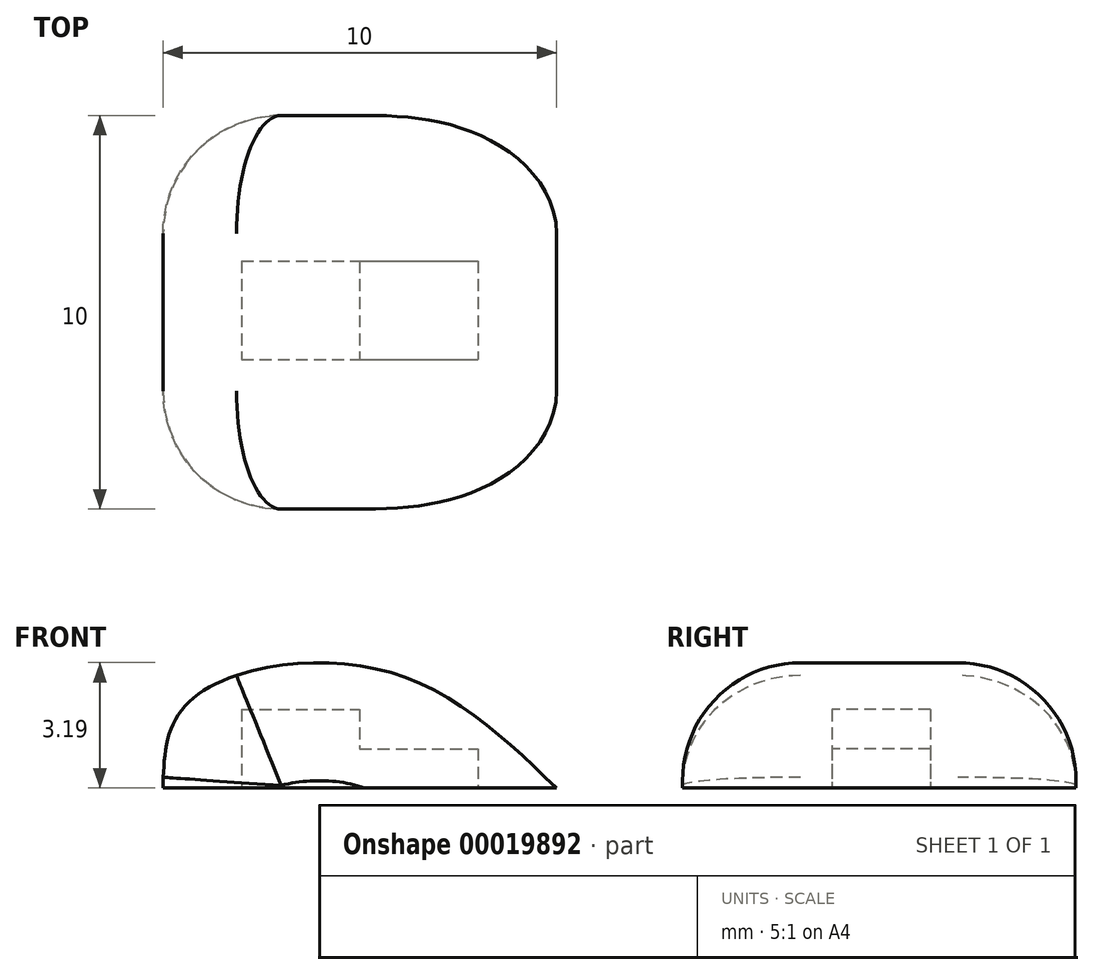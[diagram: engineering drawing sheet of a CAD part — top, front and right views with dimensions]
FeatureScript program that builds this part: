
annotation { "Feature Type Name" : "Feature", "Feature Type Description" : "" }
export const myFeature = defineFeature(function(context is Context, id is Id, definition is map)
    precondition{}
    {
        {
            var Q0;
            Q0=qCreatedBy(makeId("Front.planeOp"),FACE);
            var sketch = newSketch(context, id + "F0", { "sketchPlane" : qUnion([Q0])});
            skLineSegment(sketch, "E0", {"start": v(-11.41, -9.36) * mm, "end": v(-1.41, -9.36) * mm});
            skFitSpline(sketch, "E1", {"points": [v(-11.41, -9.36) * mm, v(-10.74, -7.16) * mm, v(-5.93, -6.34) * mm, v(-1.41, -9.36) * mm], "startDerivative": vector(0.3, 9.7) * mm, "endDerivative": vector(10.47, -10.1) * mm});
            skSolve(sketch);
        }
        {
            var Q0;
            Q0=makeQuery(id+"F0.imprint","IMPRINT",FACE,{"disambiguationData":[TD([[makeQuery(id+"F0.imprint","IMPRINT",EDGE,{"derivedFrom":sQuery(id+"F0.wireOp",EDGE,"E0")}),1.0]])]});
            extrude(context, id + "F1", {"entities" : qUnion([Q0]), "depth" : 10 * mm});
        }
        {
            var Q0;
            Q0=makeQuery(id+"F1.opExtrude","CAP_EDGE",EDGE,{"disambiguationData":[OSD([sQuery(id+"F0.wireOp",EDGE,"E1")])],"isStart":false});
            fillet(context, id + "F2", {"entities" : qUnion([Q0]), "radius" : 3 * mm, "tangentPropagation" : true, "allowEdgeOverflow" : false});
        }
        {
            var Q0;
            Q0=makeQuery(id+"F1.opExtrude","CAP_EDGE",EDGE,{"disambiguationData":[OSD([sQuery(id+"F0.wireOp",EDGE,"E1")])],"isStart":true});
            fillet(context, id + "F3", {"entities" : qUnion([Q0]), "radius" : 3 * mm, "tangentPropagation" : true, "allowEdgeOverflow" : false});
        }
        {
            var Q0;
            Q0=makeQuery(id+"F1.opExtrude","SWEPT_FACE",FACE,{"disambiguationData":[OSD([sQuery(id+"F0.wireOp",EDGE,"E0")])]});
            var sketch = newSketch(context, id + "F4", { "sketchPlane" : qUnion([Q0])});
            skLineSegment(sketch, "E2.bottom", {"start": v(-9.41, 3.7) * mm, "end": v(-3.41, 3.7) * mm});
            skLineSegment(sketch, "E2.top", {"start": v(-9.41, 6.2) * mm, "end": v(-3.41, 6.2) * mm});
            skLineSegment(sketch, "E2.left", {"start": v(-9.41, 3.7) * mm, "end": v(-9.41, 6.2) * mm});
            skLineSegment(sketch, "E2.right", {"start": v(-3.41, 3.7) * mm, "end": v(-3.41, 6.2) * mm});
            skSolve(sketch);
        }
        {
            var Q0;
            Q0=makeQuery(id+"F4.imprint","IMPRINT",FACE,{"disambiguationData":[TD([[makeQuery(id+"F4.imprint","IMPRINT",EDGE,{"derivedFrom":sQuery(id+"F4.wireOp",EDGE,"E2.bottom")}),1.0]])]});
            extrude(context, id + "F5", {"entities" : qUnion([Q0]), "operationType" : NewBodyOperationType.REMOVE, "oppositeDirection" : true, "depth" : 1 * mm});
        }
        {
            var Q0;
            Q0=makeQuery(id+"F5.boolean.opBoolean","COPY",FACE,{"derivedFrom":makeQuery(id+"F5.opExtrude","CAP_FACE",FACE,{"disambiguationData":[OSD([sQuery(id+"F4.wireOp",EDGE,"E2.bottom"),sQuery(id+"F4.wireOp",EDGE,"E2.top"),sQuery(id+"F4.wireOp",EDGE,"E2.left"),sQuery(id+"F4.wireOp",EDGE,"E2.right")])],"isStart":false})});
            var sketch = newSketch(context, id + "F6", { "sketchPlane" : qUnion([Q0])});
            skLineSegment(sketch, "E3.bottom", {"start": v(-9.41, 3.7) * mm, "end": v(-6.41, 3.7) * mm});
            skLineSegment(sketch, "E3.top", {"start": v(-9.41, 6.2) * mm, "end": v(-6.41, 6.2) * mm});
            skLineSegment(sketch, "E3.left", {"start": v(-9.41, 3.7) * mm, "end": v(-9.41, 6.2) * mm});
            skLineSegment(sketch, "E3.right", {"start": v(-6.41, 3.7) * mm, "end": v(-6.41, 6.2) * mm});
            skSolve(sketch);
        }
        {
            var Q0;
            Q0=makeQuery(id+"F6.imprint","IMPRINT",FACE,{"disambiguationData":[TD([[makeQuery(id+"F6.imprint","IMPRINT",EDGE,{"derivedFrom":sQuery(id+"F6.wireOp",EDGE,"E3.bottom")}),1.0]])]});
            extrude(context, id + "F7", {"entities" : qUnion([Q0]), "operationType" : NewBodyOperationType.REMOVE, "oppositeDirection" : true, "depth" : 1 * mm});
        }
    });
